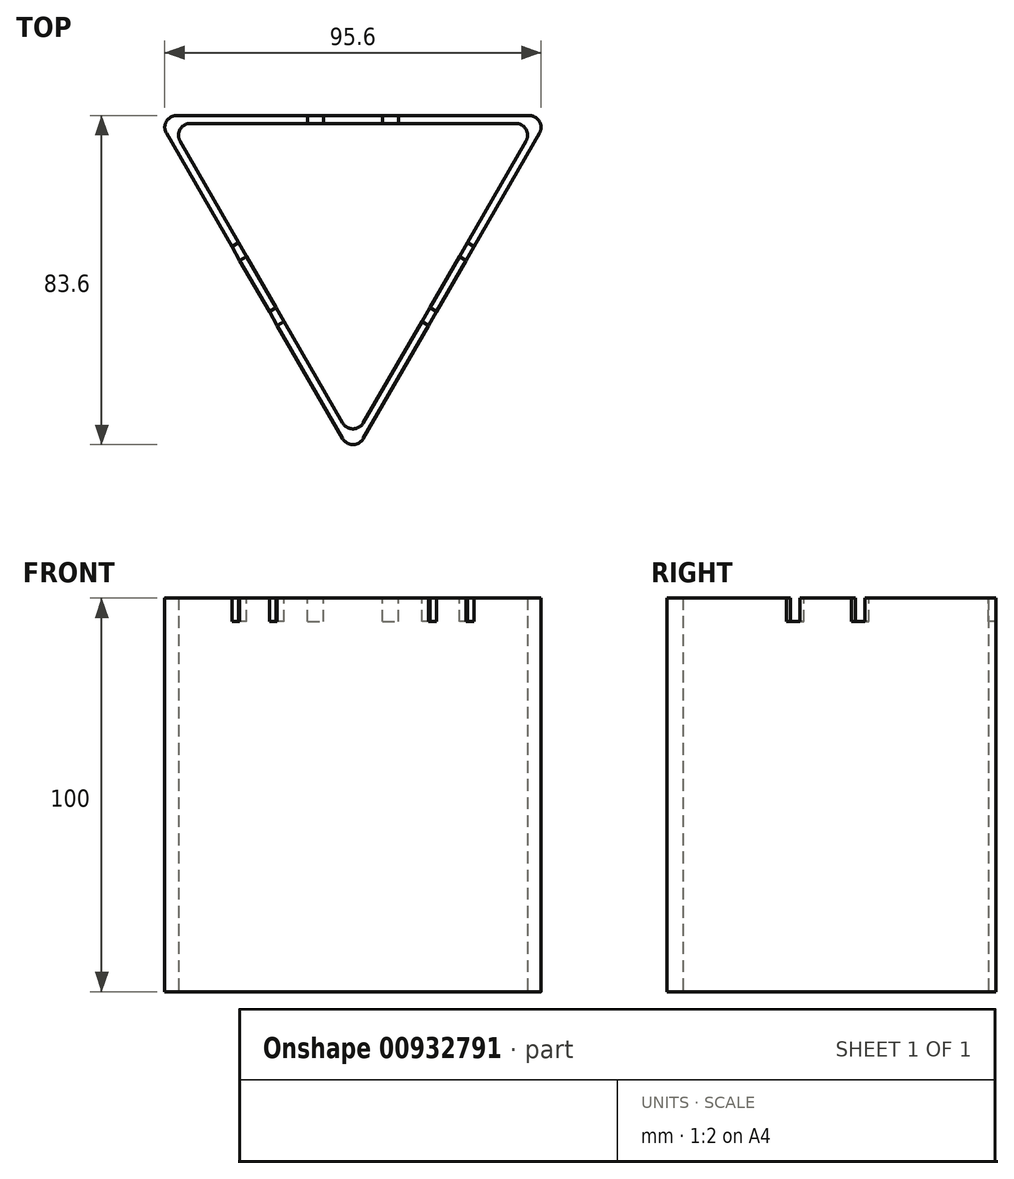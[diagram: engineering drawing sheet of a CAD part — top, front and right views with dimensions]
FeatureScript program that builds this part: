
annotation { "Feature Type Name" : "Feature", "Feature Type Description" : "" }
export const myFeature = defineFeature(function(context is Context, id is Id, definition is map)
    precondition{}
    {
        {
            var Q0;
            Q0=qCreatedBy(makeId("Top.planeOp"),FACE);
            var sketch = newSketch(context, id + "F0", { "sketchPlane" : qUnion([Q0])});
            skLineSegment(sketch, "E0", {"start": v(-13.58, 21.01) * mm, "end": v(76.02, 21.01) * mm});
            skLineSegment(sketch, "E1", {"start": v(78.62, 16.51) * mm, "end": v(33.82, -61.1) * mm});
            skLineSegment(sketch, "E2", {"start": v(28.62, -61.1) * mm, "end": v(-16.18, 16.51) * mm});
            skLineSegment(sketch, "E3.0", {"start": v(-10.12, 19.01) * mm, "end": v(72.56, 19.01) * mm});
            skLineSegment(sketch, "E3.1", {"start": v(28.62, -57.1) * mm, "end": v(-12.72, 14.51) * mm});
            skLineSegment(sketch, "E3.2", {"start": v(75.16, 14.51) * mm, "end": v(33.82, -57.1) * mm});
            skPoint(sketch, "E4.visualSharp", {"position": v(-15.32, 19.01) * mm});
            skArc(sketch, "E4.filletArc", {"start": v(-10.12, 19.01) * mm, "mid": v(-12.72, 17.51) * mm, "end": v(-12.72, 14.51) * mm});
            skPoint(sketch, "E5.visualSharp", {"position": v(77.75, 19.01) * mm});
            skArc(sketch, "E5.filletArc", {"start": v(75.16, 14.51) * mm, "mid": v(75.16, 17.51) * mm, "end": v(72.56, 19.01) * mm});
            skPoint(sketch, "E6.visualSharp", {"position": v(31.22, -61.6) * mm});
            skArc(sketch, "E6.filletArc", {"start": v(28.62, -57.1) * mm, "mid": v(31.22, -58.6) * mm, "end": v(33.82, -57.1) * mm});
            skPoint(sketch, "E7.visualSharp", {"position": v(-18.78, 21.01) * mm});
            skArc(sketch, "E7.filletArc", {"start": v(-13.58, 21.01) * mm, "mid": v(-16.18, 19.51) * mm, "end": v(-16.18, 16.51) * mm});
            skPoint(sketch, "E8.visualSharp", {"position": v(81.22, 21.01) * mm});
            skArc(sketch, "E8.filletArc", {"start": v(78.62, 16.51) * mm, "mid": v(78.62, 19.51) * mm, "end": v(76.02, 21.01) * mm});
            skPoint(sketch, "E9.visualSharp", {"position": v(31.22, -65.6) * mm});
            skArc(sketch, "E9.filletArc", {"start": v(28.62, -61.1) * mm, "mid": v(31.22, -62.6) * mm, "end": v(33.82, -61.1) * mm});
            skSolve(sketch);
        }
        {
            var Q0;
            Q0 = qSketchRegion(id + "F0", true);
            extrude(context, id + "F1", {"entities" : qUnion([Q0]), "depth" : 100 * mm, "offsetDistance" : 25 * mm});
        }
        {
            var Q0;
            Q0=makeQuery(id+"F1.opExtrude","CAP_FACE",FACE,{"disambiguationData":[OSD([sQuery(id+"F0.wireOp",EDGE,"E0"),sQuery(id+"F0.wireOp",EDGE,"E1"),sQuery(id+"F0.wireOp",EDGE,"E2"),sQuery(id+"F0.wireOp",EDGE,"E3.0"),sQuery(id+"F0.wireOp",EDGE,"E3.1"),sQuery(id+"F0.wireOp",EDGE,"E3.2"),sQuery(id+"F0.wireOp",EDGE,"E4.filletArc"),sQuery(id+"F0.wireOp",EDGE,"E5.filletArc"),sQuery(id+"F0.wireOp",EDGE,"E6.filletArc"),sQuery(id+"F0.wireOp",EDGE,"E7.filletArc"),sQuery(id+"F0.wireOp",EDGE,"E8.filletArc"),sQuery(id+"F0.wireOp",EDGE,"E9.filletArc")])],"isStart":false});
            var sketch = newSketch(context, id + "F2", { "sketchPlane" : qUnion([Q0])});
            skLineSegment(sketch, "E10.bottom", {"start": v(19.67, 21.01) * mm, "end": v(23.72, 21.01) * mm});
            skLineSegment(sketch, "E10.top", {"start": v(19.67, 19.01) * mm, "end": v(23.72, 19.01) * mm});
            skLineSegment(sketch, "E10.left", {"start": v(19.67, 21.01) * mm, "end": v(19.67, 19.01) * mm});
            skLineSegment(sketch, "E10.right", {"start": v(23.72, 21.01) * mm, "end": v(23.72, 19.01) * mm});
            skLineSegment(sketch, "E11.bottom", {"start": v(38.72, 21.01) * mm, "end": v(42.77, 21.01) * mm});
            skLineSegment(sketch, "E11.top", {"start": v(38.72, 19.01) * mm, "end": v(42.77, 19.01) * mm});
            skLineSegment(sketch, "E11.left", {"start": v(38.72, 21.01) * mm, "end": v(38.72, 19.01) * mm});
            skLineSegment(sketch, "E11.right", {"start": v(42.77, 21.01) * mm, "end": v(42.77, 19.01) * mm});
            skLineSegment(sketch, "E12", {"start": v(0.44, -12.29) * mm, "end": v(2.18, -11.29) * mm});
            skLineSegment(sketch, "E13", {"start": v(2.18, -11.29) * mm, "end": v(4.2, -14.8) * mm});
            skLineSegment(sketch, "E14", {"start": v(4.2, -14.8) * mm, "end": v(2.47, -15.8) * mm});
            skLineSegment(sketch, "E15", {"start": v(2.47, -15.8) * mm, "end": v(0.44, -12.29) * mm});
            skLineSegment(sketch, "E16", {"start": v(9.97, -28.78) * mm, "end": v(11.7, -27.78) * mm});
            skLineSegment(sketch, "E17", {"start": v(11.7, -27.78) * mm, "end": v(13.73, -31.3) * mm});
            skLineSegment(sketch, "E18", {"start": v(13.73, -31.3) * mm, "end": v(12, -32.3) * mm});
            skLineSegment(sketch, "E19", {"start": v(12, -32.3) * mm, "end": v(9.97, -28.78) * mm});
            skLineSegment(sketch, "E20", {"start": v(60.26, -11.29) * mm, "end": v(62, -12.29) * mm});
            skLineSegment(sketch, "E21", {"start": v(62, -12.29) * mm, "end": v(59.97, -15.8) * mm});
            skLineSegment(sketch, "E22", {"start": v(59.97, -15.8) * mm, "end": v(58.24, -14.8) * mm});
            skLineSegment(sketch, "E23", {"start": v(58.24, -14.8) * mm, "end": v(60.26, -11.29) * mm});
            skLineSegment(sketch, "E24", {"start": v(50.74, -27.78) * mm, "end": v(52.47, -28.78) * mm});
            skLineSegment(sketch, "E25", {"start": v(52.47, -28.78) * mm, "end": v(50.44, -32.3) * mm});
            skLineSegment(sketch, "E26", {"start": v(50.44, -32.3) * mm, "end": v(48.71, -31.3) * mm});
            skLineSegment(sketch, "E27", {"start": v(48.71, -31.3) * mm, "end": v(50.74, -27.78) * mm});
            skSolve(sketch);
        }
        {
            var Q0;
            Q0 = qSketchRegion(id + "F2", true);
            extrude(context, id + "F3", {"entities" : qUnion([Q0]), "operationType" : NewBodyOperationType.REMOVE, "oppositeDirection" : true, "depth" : 6 * mm, "offsetDistance" : 25 * mm});
        }
    });
